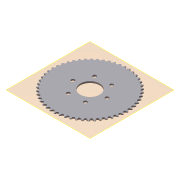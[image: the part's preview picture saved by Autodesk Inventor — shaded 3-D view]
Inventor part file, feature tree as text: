
AUTODESK INVENTOR PART (.ipt)
format: ipt  version: 2011 (Build 150239000, 239)  size: 1,264,128 bytes
history: native  units: mm
features: other x7, extrude x3, sketch x2, pattern_linear x1, pattern_circular x1, hole x1
ambient origin geometry x8: Origin, YZ Plane, XZ Plane, XY Plane, X Axis, Y Axis, Z Axis, Center Point
bodies: Solid1 (feature_tree)
feature tree (15):
  other  "25 sprocket 54T"
  other  "Theoretical Tooth Profile"
  other  "Tooth Profile"
  other  "Section Profile"
  other  "Shroud"
  other  "Strand"
  pattern_linear  "Strand Pattern"  Spacing1=1.697355mm  [1 undecoded]
  extrude  "Theoretical Tooth"  Depth=22.010541mm
  extrude  "Tooth"  Depth=2.960596mm
  pattern_circular  "Tooth Pattern"  [2 undecoded]
  other  "Timing Plane"
  extrude  "Extrusion4"  Depth=4.338955mm
  hole  "Hole2"  [1 undecoded]
  sketch  "Sketch4"  dims[d0=109.210056mm]
  sketch  "Sketch6"  dims[d2=1.163553mm d3=1.697355mm d10=22.010541mm d11=2.960596mm d12=2.6416mm d13=4.338955mm d14=4.6228mm d18=10.0mm d19=0.0mm d20=540.0mm d21=360.0deg d23=1.905mm d28=0.0mm d29=0.0mm d30=2.286mm d31=64.960832mm d32=2.286mm d33=0.79375mm d34=6.75005mm d36=90.0deg d37=90.0deg d38=10.0mm d40=6.4008mm d42=0.0mm d43=1.143mm d44=23.998278mm d45=1.697355mm d46=15.05712mm d47=0.0mm d48=25.4mm d49=0.0mm d50=10.0mm d52=25.4mm d53=0.0mm d67=28.5623mm d68=47.625mm d69=5.2324mm d70=60.0mm d72=360.0deg d74=5.2324mm d75=19.05mm d76=9.525mm d77=6.35mm d78=14.3117mm d79=25.4mm d80=20.594885mm]
note: 4 required parameter values undecoded (feature->parameter linkage not recoverable at this tier; creation-order binding heuristic only, values carry confidence <= 0.55)
